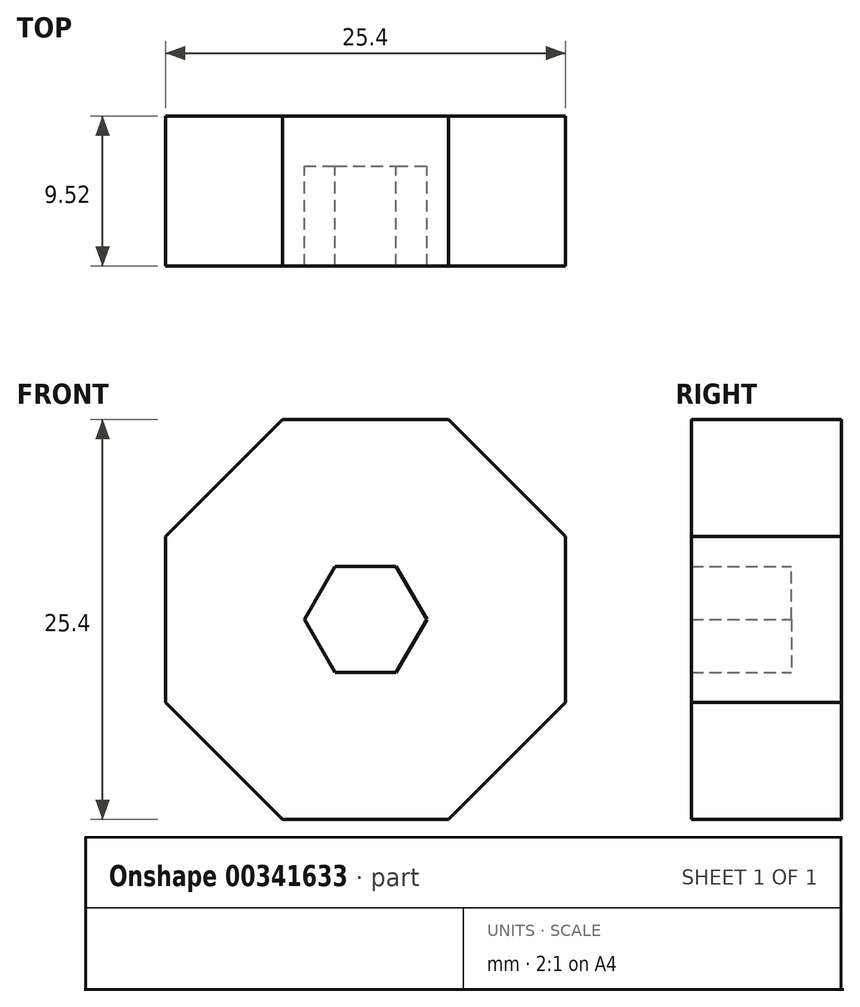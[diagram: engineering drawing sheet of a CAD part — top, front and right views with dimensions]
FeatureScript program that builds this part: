
annotation { "Feature Type Name" : "Feature", "Feature Type Description" : "" }
export const myFeature = defineFeature(function(context is Context, id is Id, definition is map)
    precondition{}
    {
        {
            var Q0;
            Q0=qCreatedBy(makeId("Front.planeOp"),FACE);
            var sketch = newSketch(context, id + "F0", { "sketchPlane" : qUnion([Q0])});
            skCircle(sketch, "E0.cCircle", {"center": v(0, 0) * mm, "radius": 12.7 * mm, "construction": true});
            skLineSegment(sketch, "E0.0", {"start": v(-5.26, 12.7) * mm, "end": v(5.26, 12.7) * mm});
            skLineSegment(sketch, "E0.1", {"start": v(5.26, 12.7) * mm, "end": v(12.7, 5.26) * mm});
            skLineSegment(sketch, "E0.2", {"start": v(12.7, 5.26) * mm, "end": v(12.7, -5.26) * mm});
            skLineSegment(sketch, "E0.3", {"start": v(12.7, -5.26) * mm, "end": v(5.26, -12.7) * mm});
            skLineSegment(sketch, "E0.4", {"start": v(5.26, -12.7) * mm, "end": v(-5.26, -12.7) * mm});
            skLineSegment(sketch, "E0.5", {"start": v(-5.26, -12.7) * mm, "end": v(-12.7, -5.26) * mm});
            skLineSegment(sketch, "E0.6", {"start": v(-12.7, -5.26) * mm, "end": v(-12.7, 5.26) * mm});
            skLineSegment(sketch, "E0.7", {"start": v(-12.7, 5.26) * mm, "end": v(-5.26, 12.7) * mm});
            skPoint(sketch, "E0.0.midPoint", {"position": v(0, 12.7) * mm});
            skSolve(sketch);
        }
        {
            var Q0;
            Q0=makeQuery(id+"F0.imprint","IMPRINT",FACE,{"disambiguationData":[TD([[makeQuery(id+"F0.imprint","IMPRINT",EDGE,{"derivedFrom":sQuery(id+"F0.wireOp",EDGE,"E0.0")}),-1.0]])]});
            var Q1;
            Q1=sQuery(id+"F0.wireOp",EDGE,"e404a271-6062-4685-87c1-b4208ab16462.1");
            extrude(context, id + "F1", {"entities" : qUnion([Q0]), "surfaceEntities" : qUnion([Q1]), "oppositeDirection" : true, "depth" : 3.17 * mm});
        }
        {
            var Q0;
            Q0=makeQuery(id+"F1.opExtrude","CAP_FACE",FACE,{"disambiguationData":[OSD([sQuery(id+"F0.wireOp",EDGE,"E0.0"),sQuery(id+"F0.wireOp",EDGE,"E0.1"),sQuery(id+"F0.wireOp",EDGE,"E0.2"),sQuery(id+"F0.wireOp",EDGE,"E0.3"),sQuery(id+"F0.wireOp",EDGE,"E0.4"),sQuery(id+"F0.wireOp",EDGE,"E0.5"),sQuery(id+"F0.wireOp",EDGE,"E0.6"),sQuery(id+"F0.wireOp",EDGE,"E0.7")])],"isStart":true});
            var sketch = newSketch(context, id + "F2", { "sketchPlane" : qUnion([Q0])});
            skCircle(sketch, "E1.cCircle", {"center": v(0, 0) * mm, "radius": 3.37 * mm, "construction": true});
            skLineSegment(sketch, "E1.0", {"start": v(-1.94, 3.37) * mm, "end": v(1.94, 3.37) * mm});
            skLineSegment(sketch, "E1.1", {"start": v(1.94, 3.37) * mm, "end": v(3.89, 0) * mm});
            skLineSegment(sketch, "E1.2", {"start": v(3.89, 0) * mm, "end": v(1.94, -3.37) * mm});
            skLineSegment(sketch, "E1.3", {"start": v(1.94, -3.37) * mm, "end": v(-1.94, -3.37) * mm});
            skLineSegment(sketch, "E1.4", {"start": v(-1.94, -3.37) * mm, "end": v(-3.89, 0) * mm});
            skLineSegment(sketch, "E1.5", {"start": v(-3.89, 0) * mm, "end": v(-1.94, 3.37) * mm});
            skPoint(sketch, "E1.0.midPoint", {"position": v(0, 3.37) * mm});
            skSolve(sketch);
        }
        {
            var Q0;
            Q0=makeQuery(id+"F2.imprint","IMPRINT",FACE,{"disambiguationData":[TD([[makeQuery(id+"F2.imprint","IMPRINT",EDGE,{"derivedFrom":sQuery(id+"F2.wireOp",EDGE,"E1.0")}),1.0]])]});
            extrude(context, id + "F3", {"entities" : qUnion([Q0]), "operationType" : NewBodyOperationType.ADD, "depth" : 6.35 * mm});
        }
    });
